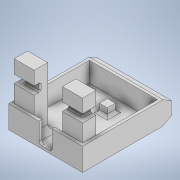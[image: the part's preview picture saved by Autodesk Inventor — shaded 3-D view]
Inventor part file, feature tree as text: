
AUTODESK INVENTOR PART (.ipt)
format: ipt  version: 2021 (Build 250183000, 183)  size: 189,440 bytes
history: native  units: mm
features: extrude x1, sketch x1
ambient origin geometry x8: Origin, YZ Plane, XZ Plane, XY Plane, X Axis, Y Axis, Z Axis, Center Point
bodies: Solid2 (feature_tree), Solid1 (feature_tree)
feature tree (2):
  extrude  "Extrusion1"  Depth=10.0mm
  sketch  "Sketch1"  dims[d0=60.0deg d1=10.0mm d2=10.0mm d3=0.0mm]
